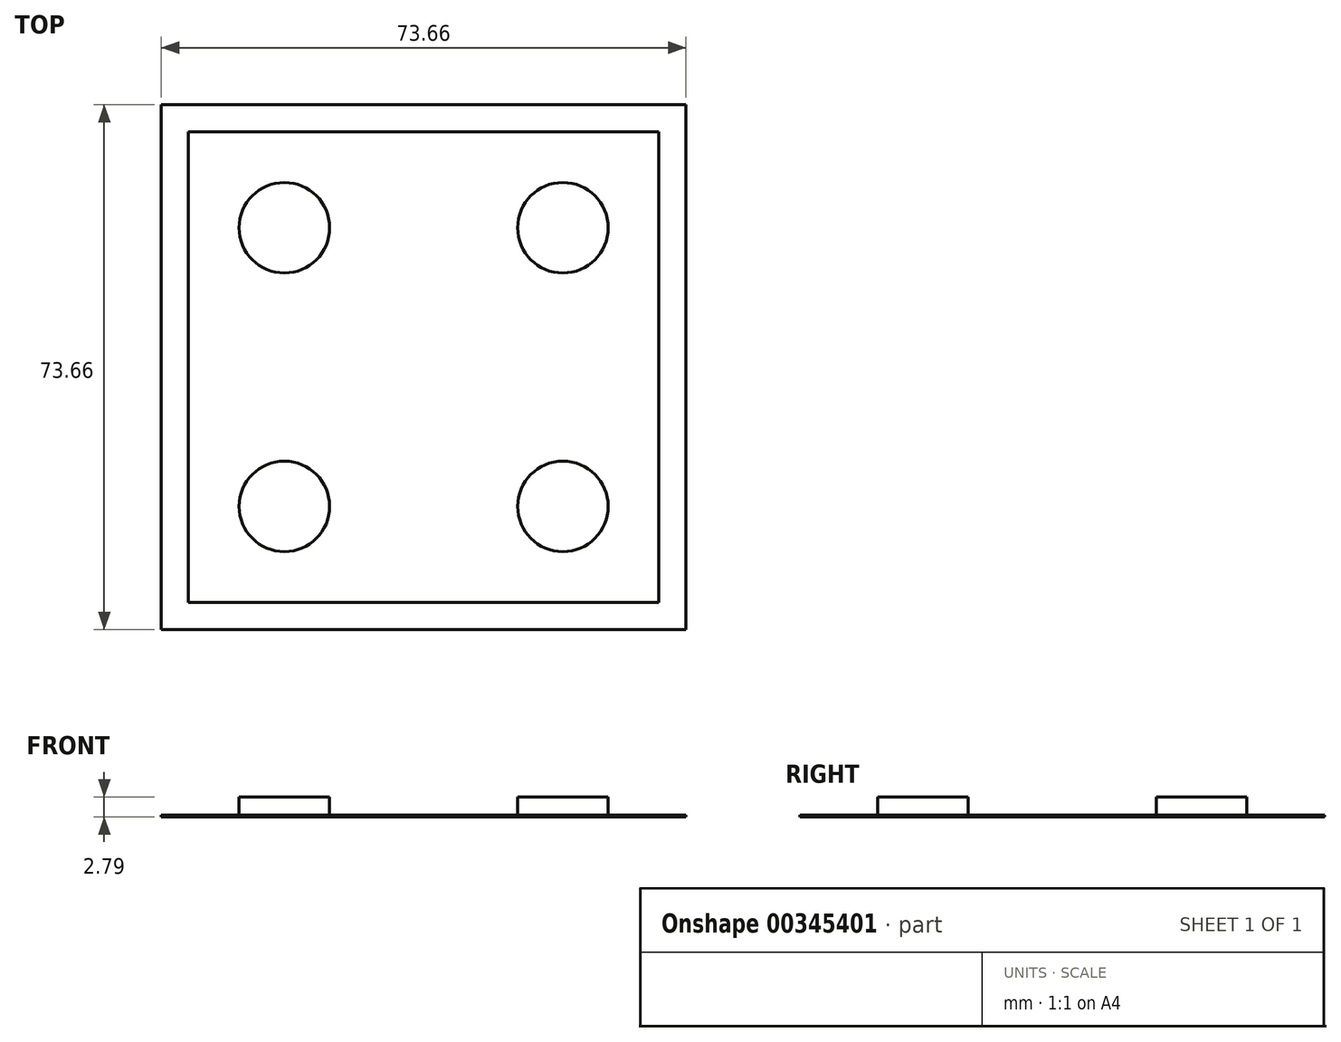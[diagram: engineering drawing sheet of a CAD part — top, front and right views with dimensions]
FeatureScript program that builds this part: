
annotation { "Feature Type Name" : "Feature", "Feature Type Description" : "" }
export const myFeature = defineFeature(function(context is Context, id is Id, definition is map)
    precondition{}
    {
        {
            var Q0;
            Q0=qCreatedBy(makeId("Top.planeOp"),FACE);
            var sketch = newSketch(context, id + "F0", { "sketchPlane" : qUnion([Q0])});
            skLineSegment(sketch, "E0.bottom", {"start": v(0, 0) * mm, "end": v(73.66, 0) * mm});
            skLineSegment(sketch, "E0.top", {"start": v(0, 73.66) * mm, "end": v(73.66, 73.66) * mm});
            skLineSegment(sketch, "E0.left", {"start": v(0, 0) * mm, "end": v(0, 73.66) * mm});
            skLineSegment(sketch, "E0.right", {"start": v(73.66, 0) * mm, "end": v(73.66, 73.66) * mm});
            skSolve(sketch);
        }
        {
            var Q0;
            Q0=qSketchRegion(id+"F0",true);
            extrude(context, id + "F1", {"entities" : qUnion([Q0]), "depth" : 0.25 * mm});
        }
        {
            var Q0;
            Q0=makeQuery(id+"F1.opExtrude","CAP_FACE",FACE,{"disambiguationData":[OSD([sQuery(id+"F0.wireOp",EDGE,"E0.bottom"),sQuery(id+"F0.wireOp",EDGE,"E0.top"),sQuery(id+"F0.wireOp",EDGE,"E0.left"),sQuery(id+"F0.wireOp",EDGE,"E0.right")])],"isStart":false});
            var sketch = newSketch(context, id + "F2", { "sketchPlane" : qUnion([Q0])});
            skLineSegment(sketch, "E1.bottom", {"start": v(0, 73.66) * mm, "end": v(73.66, 73.66) * mm});
            skLineSegment(sketch, "E1.top", {"start": v(0, 0) * mm, "end": v(73.66, 0) * mm});
            skLineSegment(sketch, "E1.left", {"start": v(0, 73.66) * mm, "end": v(0, 0) * mm});
            skLineSegment(sketch, "E1.right", {"start": v(73.66, 73.66) * mm, "end": v(73.66, 0) * mm});
            skLineSegment(sketch, "E2.bottom", {"start": v(3.81, 69.85) * mm, "end": v(69.85, 69.85) * mm});
            skLineSegment(sketch, "E2.top", {"start": v(3.81, 3.81) * mm, "end": v(69.85, 3.81) * mm});
            skLineSegment(sketch, "E2.left", {"start": v(3.81, 69.85) * mm, "end": v(3.81, 3.81) * mm});
            skLineSegment(sketch, "E2.right", {"start": v(69.85, 69.85) * mm, "end": v(69.85, 3.81) * mm});
            skSolve(sketch);
        }
        {
            var Q0;
            Q0=qSketchRegion(id+"F2",true);
            extrude(context, id + "F3", {"entities" : qUnion([Q0]), "operationType" : NewBodyOperationType.ADD, "depth" : 0.03 * mm});
        }
        {
            var Q0;
            Q0=makeQuery(id+"F1.opExtrude","CAP_FACE",FACE,{"disambiguationData":[OSD([sQuery(id+"F0.wireOp",EDGE,"E0.bottom"),sQuery(id+"F0.wireOp",EDGE,"E0.top"),sQuery(id+"F0.wireOp",EDGE,"E0.left"),sQuery(id+"F0.wireOp",EDGE,"E0.right")])],"isStart":false});
            var sketch = newSketch(context, id + "F4", { "sketchPlane" : qUnion([Q0])});
            skLineSegment(sketch, "E3", {"start": v(3.8, 69.85) * mm, "end": v(69.85, 3.8) * mm, "construction": true});
            skLineSegment(sketch, "E4", {"start": v(3.8, 3.8) * mm, "end": v(69.85, 69.85) * mm, "construction": true});
            skCircle(sketch, "E5", {"center": v(17.28, 56.38) * mm, "radius": 6.35 * mm});
            skLineSegment(sketch, "E6", {"start": v(3.81, 36.83) * mm, "end": v(69.85, 36.83) * mm, "construction": true});
            skCircle(sketch, "E7.MirrorC", {"center": v(17.28, 17.28) * mm, "radius": 6.35 * mm});
            skLineSegment(sketch, "E8", {"start": v(36.83, 69.85) * mm, "end": v(36.83, 3.8) * mm, "construction": true});
            skCircle(sketch, "E9.MirrorC", {"center": v(56.38, 17.28) * mm, "radius": 6.35 * mm});
            skCircle(sketch, "E10.MirrorC", {"center": v(56.38, 56.38) * mm, "radius": 6.35 * mm});
            skSolve(sketch);
        }
        {
            var Q0;
            Q0=qSketchRegion(id+"F4",true);
            extrude(context, id + "F5", {"entities" : qUnion([Q0]), "operationType" : NewBodyOperationType.ADD, "depth" : 2.54 * mm});
        }
    });
